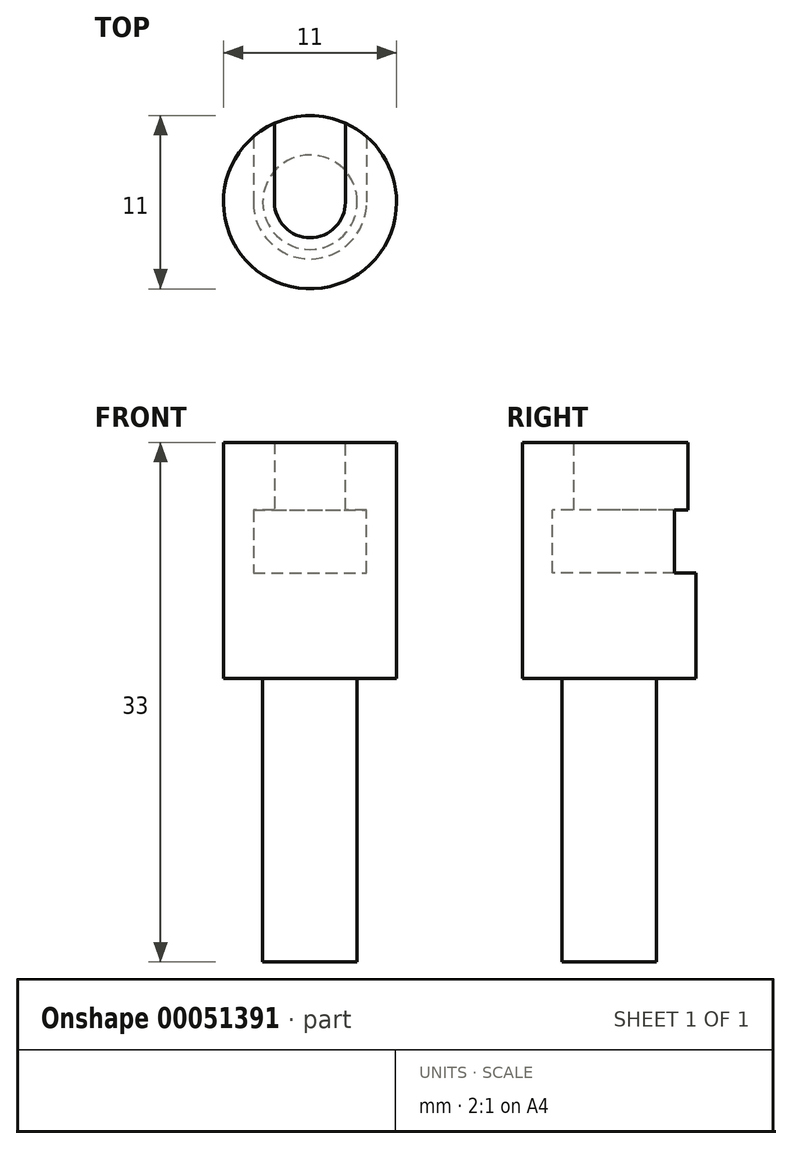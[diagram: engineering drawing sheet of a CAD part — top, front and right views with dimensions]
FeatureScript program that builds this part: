
annotation { "Feature Type Name" : "Feature", "Feature Type Description" : "" }
export const myFeature = defineFeature(function(context is Context, id is Id, definition is map)
    precondition{}
    {
        {
            var Q0;
            Q0=qCreatedBy(makeId("Front.planeOp"),FACE);
            var sketch = newSketch(context, id + "F0", { "sketchPlane" : qUnion([Q0])});
            skLineSegment(sketch, "E0", {"start": v(0, 6.7) * mm, "end": v(0, -18) * mm});
            skLineSegment(sketch, "E1", {"start": v(-3, 0) * mm, "end": v(-5.5, 0) * mm});
            skLineSegment(sketch, "E2.0", {"start": v(-2.25, 15) * mm, "end": v(-5.5, 15) * mm});
            skLineSegment(sketch, "E3.0", {"start": v(-5.5, 15) * mm, "end": v(-5.5, 0) * mm});
            skLineSegment(sketch, "E4.0", {"start": v(0, -18) * mm, "end": v(-3, -18) * mm});
            skLineSegment(sketch, "E5.0", {"start": v(-3, 0) * mm, "end": v(-3, -18) * mm});
            skLineSegment(sketch, "E6.0", {"start": v(-2.25, 15) * mm, "end": v(-2.25, 10.7) * mm});
            skLineSegment(sketch, "E7.0", {"start": v(0, 6.7) * mm, "end": v(-3.6, 6.7) * mm});
            skLineSegment(sketch, "E8.0", {"start": v(-3.6, 10.7) * mm, "end": v(-3.6, 6.7) * mm});
            skLineSegment(sketch, "E9.trimOffspring", {"start": v(-2.25, 10.7) * mm, "end": v(-3.6, 10.7) * mm});
            skPoint(sketch, "E10.orphan", {"position": v(0, 24.69) * mm});
            skSolve(sketch);
        }
        {
            var Q0;
            Q0=makeQuery(id+"F0.imprint","IMPRINT",FACE,{"disambiguationData":[TD([[makeQuery(id+"F0.imprint","IMPRINT",EDGE,{"derivedFrom":sQuery(id+"F0.wireOp",EDGE,"E0")}),-1.0]])]});
            var Q1;
            Q1=sQuery(id+"F0.wireOp",EDGE,"E0");
            revolve(context, id + "F1", {"entities" : qUnion([Q0]), "axis" : qUnion([Q1]), "revolveType" : RevolveType.FULL});
        }
        {
            var Q0;
            Q0=qCreatedBy(makeId("Front.planeOp"),FACE);
            var sketch = newSketch(context, id + "F2", { "sketchPlane" : qUnion([Q0])});
            skLineSegment(sketch, "E11", {"start": v(5.5, 15) * mm, "end": v(5.5, 0) * mm});
            skLineSegment(sketch, "E12", {"start": v(-5.5, 0) * mm, "end": v(-5.5, 15) * mm});
            skPoint(sketch, "E13", {"position": v(2.25, 15) * mm});
            skPoint(sketch, "E14", {"position": v(-2.25, 15) * mm});
            skPoint(sketch, "E15", {"position": v(-2.25, 10.7) * mm});
            skPoint(sketch, "E16", {"position": v(-3.6, 10.7) * mm});
            skPoint(sketch, "E17", {"position": v(-3.6, 6.7) * mm});
            skPoint(sketch, "E18", {"position": v(3.6, 6.7) * mm});
            skPoint(sketch, "E19", {"position": v(3.6, 10.7) * mm});
            skPoint(sketch, "E20", {"position": v(2.25, 10.7) * mm});
            skLineSegment(sketch, "E21", {"start": v(2.25, 15) * mm, "end": v(-2.25, 15) * mm});
            skLineSegment(sketch, "E22", {"start": v(-2.25, 15) * mm, "end": v(-2.25, 10.7) * mm});
            skLineSegment(sketch, "E23", {"start": v(-2.25, 10.7) * mm, "end": v(-3.6, 10.7) * mm});
            skLineSegment(sketch, "E24", {"start": v(-3.6, 10.7) * mm, "end": v(-3.6, 6.7) * mm});
            skLineSegment(sketch, "E25", {"start": v(-3.6, 6.7) * mm, "end": v(3.6, 6.7) * mm});
            skLineSegment(sketch, "E26", {"start": v(3.6, 6.7) * mm, "end": v(3.6, 10.7) * mm});
            skLineSegment(sketch, "E27", {"start": v(3.6, 10.7) * mm, "end": v(2.25, 10.7) * mm});
            skLineSegment(sketch, "E28", {"start": v(2.25, 10.7) * mm, "end": v(2.25, 15) * mm});
            skSolve(sketch);
        }
        {
            var Q0;
            Q0=makeQuery(id+"F2.imprint","IMPRINT",FACE,{"disambiguationData":[TD([[makeQuery(id+"F2.imprint","IMPRINT",EDGE,{"derivedFrom":sQuery(id+"F2.wireOp",EDGE,"E21")}),1.0]])]});
            extrude(context, id + "F3", {"entities" : qUnion([Q0]), "operationType" : NewBodyOperationType.REMOVE, "oppositeDirection" : true, "depth" : 6 * mm});
        }
    });
